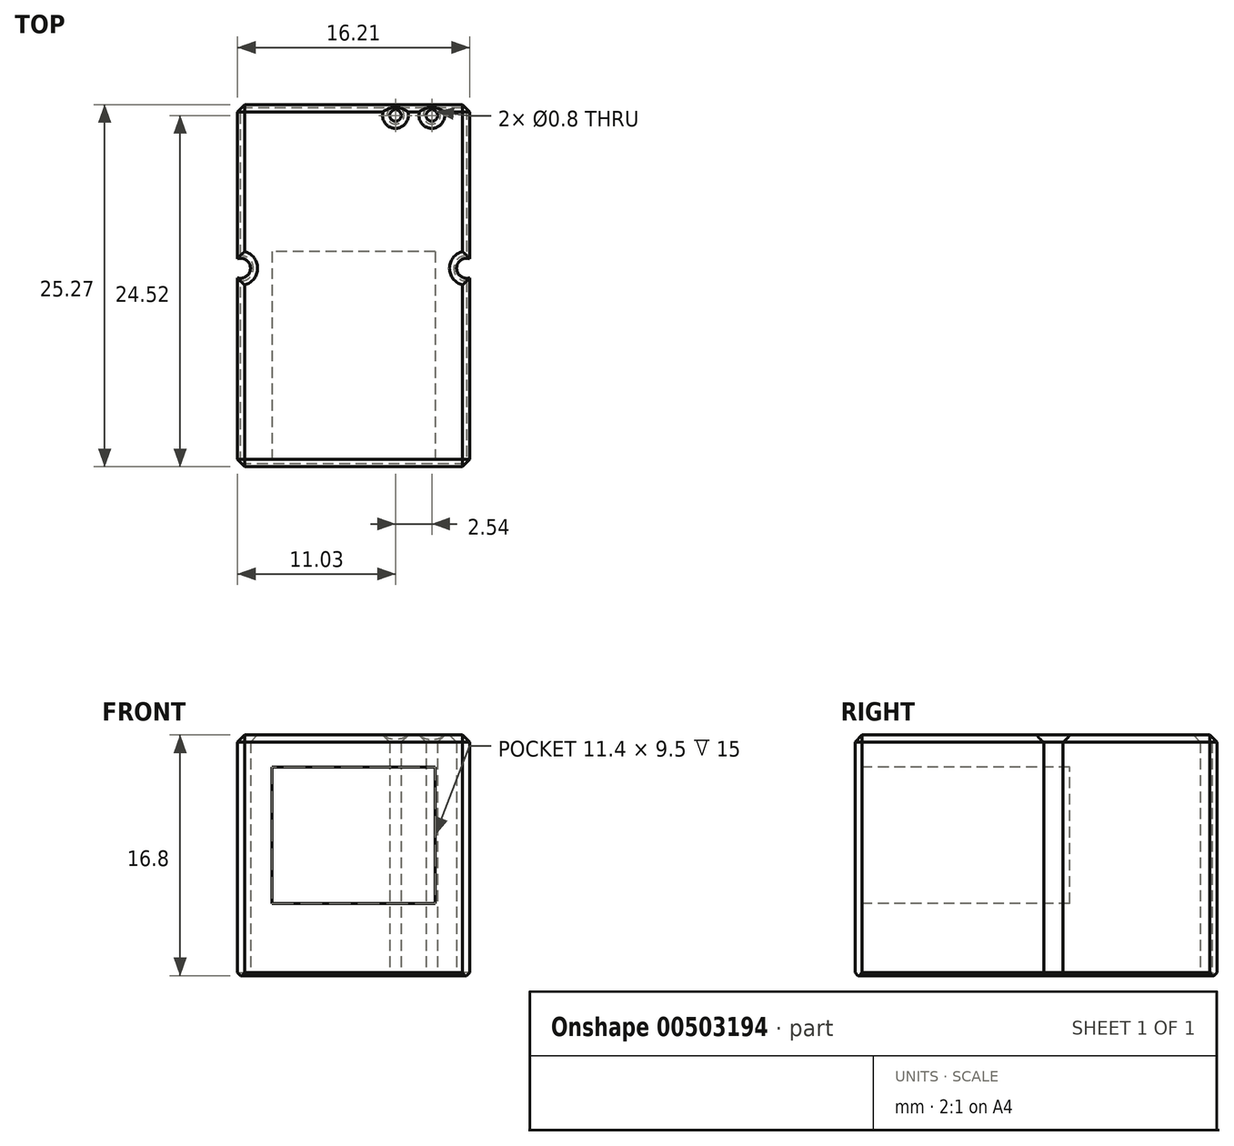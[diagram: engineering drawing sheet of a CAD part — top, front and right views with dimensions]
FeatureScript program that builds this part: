
annotation { "Feature Type Name" : "Feature", "Feature Type Description" : "" }
export const myFeature = defineFeature(function(context is Context, id is Id, definition is map)
    precondition{}
    {
        {
            var Q0;
            Q0=qCreatedBy(makeId("Top.planeOp"),FACE);
            var sketch = newSketch(context, id + "F0", { "sketchPlane" : qUnion([Q0])});
            skLineSegment(sketch, "E0.bottom", {"start": v(-12.55, 5.58) * mm, "end": v(3.66, 5.58) * mm});
            skLineSegment(sketch, "E0.top", {"start": v(-12.54, -19.7) * mm, "end": v(3.65, -19.7) * mm});
            skLineSegment(sketch, "E0.left", {"start": v(-12.54, 5.58) * mm, "end": v(-12.54, -19.7) * mm});
            skLineSegment(sketch, "E0.right", {"start": v(3.66, 5.58) * mm, "end": v(3.66, -19.7) * mm});
            skCircle(sketch, "E1", {"center": v(0, 0) * mm, "radius": 0.35 * mm});
            skCircle(sketch, "E2", {"center": v(-1.27, -2.54) * mm, "radius": 0.35 * mm});
            skLineSegment(sketch, "E3", {"start": v(-4.44, 5.58) * mm, "end": v(-4.45, -19.7) * mm, "construction": true});
            skCircle(sketch, "E4.1.0.0", {"center": v(-3.81, -2.54) * mm, "radius": 0.35 * mm});
            skCircle(sketch, "E4.1.0.1", {"center": v(-2.54, 0) * mm, "radius": 0.35 * mm});
            skCircle(sketch, "E4.2.0.0", {"center": v(-6.35, -2.54) * mm, "radius": 0.35 * mm});
            skCircle(sketch, "E4.2.0.1", {"center": v(-5.08, 0) * mm, "radius": 0.35 * mm});
            skCircle(sketch, "E4.3.0.0", {"center": v(-8.9, -2.54) * mm, "radius": 0.35 * mm});
            skCircle(sketch, "E4.3.0.1", {"center": v(-7.62, 0) * mm, "radius": 0.35 * mm});
            skLineSegment(sketch, "E4.direction1", {"start": v(-1.27, -2.54) * mm, "end": v(-3.81, -2.54) * mm, "construction": true});
            skCircle(sketch, "E5", {"center": v(-10.16, -8.9) * mm, "radius": 1.5 * mm});
            skCircle(sketch, "E6", {"center": v(1.27, -8.9) * mm, "radius": 1.5 * mm});
            skCircle(sketch, "E7", {"center": v(-12.34, -5.84) * mm, "radius": 0.7 * mm});
            skCircle(sketch, "E8", {"center": v(3.46, -5.84) * mm, "radius": 0.7 * mm});
            skPoint(sketch, "E8.centerSnap0", {"position": v(-4.44, -7.06) * mm});
            skCircle(sketch, "E9", {"center": v(-9.9, 4.83) * mm, "radius": 0.4 * mm});
            skCircle(sketch, "E10", {"center": v(-7.37, 4.83) * mm, "radius": 0.4 * mm});
            skCircle(sketch, "E11.MirrorC", {"center": v(-1.52, 4.83) * mm, "radius": 0.4 * mm});
            skCircle(sketch, "E12.MirrorC", {"center": v(1.02, 4.83) * mm, "radius": 0.4 * mm});
            skSolve(sketch);
        }
        {
            var Q0;
            {var subQ0=sQuery(id+"F0.wireOp",EDGE,"E7");var subQ1=sQuery(id+"F0.wireOp",EDGE,"E0.left");var subQ2=makeQuery(id+"F0.imprint","INTERSECT",VERTEX,{"disambiguationData":[OD(0.0)],"derivedFrom":[subQ1,subQ0]});Q0=makeQuery(id+"F0.imprint","IMPRINT",FACE,{"disambiguationData":[TD([[makeQuery(id+"F0.imprint","IMPRINT",EDGE,{"disambiguationData":[TD([[subQ2,-1.0]])],"derivedFrom":subQ1}),1.0]])]});}
            var Q1;
            {var subQ4=sQuery(id+"F0.wireOp",EDGE,"E0.bottom");Q1=makeQuery(id+"F0.imprint","IMPRINT",FACE,{"disambiguationData":[TD([[makeQuery(id+"F0.imprint","IMPRINT",EDGE,{"derivedFrom":subQ4}),-1.0]])]});}
            var Q2;
            Q2=makeQuery(id+"F0.imprint","IMPRINT",FACE,{"disambiguationData":[TD([[makeQuery(id+"F0.imprint","IMPRINT",EDGE,{"derivedFrom":sQuery(id+"F0.wireOp",EDGE,"E5")}),1.0]])]});
            var Q3;
            Q3=makeQuery(id+"F0.imprint","IMPRINT",FACE,{"disambiguationData":[TD([[makeQuery(id+"F0.imprint","IMPRINT",EDGE,{"derivedFrom":sQuery(id+"F0.wireOp",EDGE,"E6")}),1.0]])]});
            var Q4;
            {var subQ0=sQuery(id+"F0.wireOp",EDGE,"E8");var subQ1=sQuery(id+"F0.wireOp",EDGE,"E0.right");var subQ2=makeQuery(id+"F0.imprint","INTERSECT",VERTEX,{"disambiguationData":[OD(0.0)],"derivedFrom":[subQ1,subQ0]});Q4=makeQuery(id+"F0.imprint","IMPRINT",FACE,{"disambiguationData":[TD([[makeQuery(id+"F0.imprint","IMPRINT",EDGE,{"disambiguationData":[TD([[subQ2,-1.0]])],"derivedFrom":subQ1}),-1.0]])]});}
            var Q5;
            Q5=makeQuery(id+"F0.imprint","IMPRINT",FACE,{"disambiguationData":[TD([[makeQuery(id+"F0.imprint","IMPRINT",EDGE,{"derivedFrom":sQuery(id+"F0.wireOp",EDGE,"E2")}),1.0]])]});
            var Q6;
            Q6=makeQuery(id+"F0.imprint","IMPRINT",FACE,{"disambiguationData":[TD([[makeQuery(id+"F0.imprint","IMPRINT",EDGE,{"derivedFrom":sQuery(id+"F0.wireOp",EDGE,"E4.1.0.0")}),1.0]])]});
            var Q7;
            Q7=makeQuery(id+"F0.imprint","IMPRINT",FACE,{"disambiguationData":[TD([[makeQuery(id+"F0.imprint","IMPRINT",EDGE,{"derivedFrom":sQuery(id+"F0.wireOp",EDGE,"E4.2.0.0")}),1.0]])]});
            var Q8;
            Q8=makeQuery(id+"F0.imprint","IMPRINT",FACE,{"disambiguationData":[TD([[makeQuery(id+"F0.imprint","IMPRINT",EDGE,{"derivedFrom":sQuery(id+"F0.wireOp",EDGE,"E4.3.0.0")}),1.0]])]});
            var Q9;
            Q9=makeQuery(id+"F0.imprint","IMPRINT",FACE,{"disambiguationData":[TD([[makeQuery(id+"F0.imprint","IMPRINT",EDGE,{"derivedFrom":sQuery(id+"F0.wireOp",EDGE,"E4.3.0.1")}),1.0]])]});
            var Q10;
            Q10=makeQuery(id+"F0.imprint","IMPRINT",FACE,{"disambiguationData":[TD([[makeQuery(id+"F0.imprint","IMPRINT",EDGE,{"derivedFrom":sQuery(id+"F0.wireOp",EDGE,"E4.2.0.1")}),1.0]])]});
            var Q11;
            Q11=makeQuery(id+"F0.imprint","IMPRINT",FACE,{"disambiguationData":[TD([[makeQuery(id+"F0.imprint","IMPRINT",EDGE,{"derivedFrom":sQuery(id+"F0.wireOp",EDGE,"E4.1.0.1")}),1.0]])]});
            var Q12;
            Q12=makeQuery(id+"F0.imprint","IMPRINT",FACE,{"disambiguationData":[TD([[makeQuery(id+"F0.imprint","IMPRINT",EDGE,{"derivedFrom":sQuery(id+"F0.wireOp",EDGE,"E1")}),1.0]])]});
            var Q13;
            Q13=makeQuery(id+"F0.imprint","IMPRINT",FACE,{"disambiguationData":[TD([[makeQuery(id+"F0.imprint","IMPRINT",EDGE,{"derivedFrom":sQuery(id+"F0.wireOp",EDGE,"E12.MirrorC")}),-1.0]])]});
            var Q14;
            Q14=makeQuery(id+"F0.imprint","IMPRINT",FACE,{"disambiguationData":[TD([[makeQuery(id+"F0.imprint","IMPRINT",EDGE,{"derivedFrom":sQuery(id+"F0.wireOp",EDGE,"E11.MirrorC")}),-1.0]])]});
            var Q15;
            Q15=makeQuery(id+"F0.imprint","IMPRINT",FACE,{"disambiguationData":[TD([[makeQuery(id+"F0.imprint","IMPRINT",EDGE,{"derivedFrom":sQuery(id+"F0.wireOp",EDGE,"E10")}),1.0]])]});
            var Q16;
            Q16=makeQuery(id+"F0.imprint","IMPRINT",FACE,{"disambiguationData":[TD([[makeQuery(id+"F0.imprint","IMPRINT",EDGE,{"derivedFrom":sQuery(id+"F0.wireOp",EDGE,"E9")}),1.0]])]});
            extrude(context, id + "F1", {"entities" : qUnion([Q0, Q1, Q2, Q3, Q4, Q5, Q6, Q7, Q8, Q9, Q10, Q11, Q12, Q13, Q14, Q15, Q16]), "depth" : 13.5 * mm});
        }
        {
            var Q0;
            {var subQ0=sQuery(id+"F0.wireOp",EDGE,"E7");var subQ1=sQuery(id+"F0.wireOp",EDGE,"E0.left");var subQ2=makeQuery(id+"F0.imprint","INTERSECT",VERTEX,{"disambiguationData":[OD(0.0)],"derivedFrom":[subQ1,subQ0]});Q0=makeQuery(id+"F0.imprint","IMPRINT",FACE,{"disambiguationData":[TD([[makeQuery(id+"F0.imprint","IMPRINT",EDGE,{"disambiguationData":[TD([[subQ2,-1.0]])],"derivedFrom":subQ1}),1.0]])]});}
            var Q1;
            {var subQ0=sQuery(id+"F0.wireOp",EDGE,"E8");var subQ1=sQuery(id+"F0.wireOp",EDGE,"E0.right");var subQ2=makeQuery(id+"F0.imprint","INTERSECT",VERTEX,{"disambiguationData":[OD(0.0)],"derivedFrom":[subQ1,subQ0]});Q1=makeQuery(id+"F0.imprint","IMPRINT",FACE,{"disambiguationData":[TD([[makeQuery(id+"F0.imprint","IMPRINT",EDGE,{"disambiguationData":[TD([[subQ2,-1.0]])],"derivedFrom":subQ1}),-1.0]])]});}
            var Q2;
            Q2=makeQuery(id+"F0.imprint","IMPRINT",FACE,{"disambiguationData":[TD([[makeQuery(id+"F0.imprint","IMPRINT",EDGE,{"derivedFrom":sQuery(id+"F0.wireOp",EDGE,"E5")}),1.0]])]});
            var Q3;
            Q3=makeQuery(id+"F0.imprint","IMPRINT",FACE,{"disambiguationData":[TD([[makeQuery(id+"F0.imprint","IMPRINT",EDGE,{"derivedFrom":sQuery(id+"F0.wireOp",EDGE,"E6")}),1.0]])]});
            var Q4;
            Q4=makeQuery(id+"F0.imprint","IMPRINT",FACE,{"disambiguationData":[TD([[makeQuery(id+"F0.imprint","IMPRINT",EDGE,{"derivedFrom":sQuery(id+"F0.wireOp",EDGE,"E1")}),1.0]])]});
            var Q5;
            Q5=makeQuery(id+"F0.imprint","IMPRINT",FACE,{"disambiguationData":[TD([[makeQuery(id+"F0.imprint","IMPRINT",EDGE,{"derivedFrom":sQuery(id+"F0.wireOp",EDGE,"E2")}),1.0]])]});
            var Q6;
            Q6=makeQuery(id+"F0.imprint","IMPRINT",FACE,{"disambiguationData":[TD([[makeQuery(id+"F0.imprint","IMPRINT",EDGE,{"derivedFrom":sQuery(id+"F0.wireOp",EDGE,"E4.1.0.0")}),1.0]])]});
            var Q7;
            Q7=makeQuery(id+"F0.imprint","IMPRINT",FACE,{"disambiguationData":[TD([[makeQuery(id+"F0.imprint","IMPRINT",EDGE,{"derivedFrom":sQuery(id+"F0.wireOp",EDGE,"E4.1.0.1")}),1.0]])]});
            var Q8;
            Q8=makeQuery(id+"F0.imprint","IMPRINT",FACE,{"disambiguationData":[TD([[makeQuery(id+"F0.imprint","IMPRINT",EDGE,{"derivedFrom":sQuery(id+"F0.wireOp",EDGE,"E4.2.0.0")}),1.0]])]});
            var Q9;
            Q9=makeQuery(id+"F0.imprint","IMPRINT",FACE,{"disambiguationData":[TD([[makeQuery(id+"F0.imprint","IMPRINT",EDGE,{"derivedFrom":sQuery(id+"F0.wireOp",EDGE,"E4.2.0.1")}),1.0]])]});
            var Q10;
            Q10=makeQuery(id+"F0.imprint","IMPRINT",FACE,{"disambiguationData":[TD([[makeQuery(id+"F0.imprint","IMPRINT",EDGE,{"derivedFrom":sQuery(id+"F0.wireOp",EDGE,"E4.3.0.0")}),1.0]])]});
            var Q11;
            Q11=makeQuery(id+"F0.imprint","IMPRINT",FACE,{"disambiguationData":[TD([[makeQuery(id+"F0.imprint","IMPRINT",EDGE,{"derivedFrom":sQuery(id+"F0.wireOp",EDGE,"E4.3.0.1")}),1.0]])]});
            var Q12;
            Q12=makeQuery(id+"F0.imprint","IMPRINT",FACE,{"disambiguationData":[TD([[makeQuery(id+"F0.imprint","IMPRINT",EDGE,{"derivedFrom":sQuery(id+"F0.wireOp",EDGE,"E11.MirrorC")}),-1.0]])]});
            var Q13;
            Q13=makeQuery(id+"F0.imprint","IMPRINT",FACE,{"disambiguationData":[TD([[makeQuery(id+"F0.imprint","IMPRINT",EDGE,{"derivedFrom":sQuery(id+"F0.wireOp",EDGE,"E12.MirrorC")}),-1.0]])]});
            var Q14;
            Q14=makeQuery(id+"F0.imprint","IMPRINT",FACE,{"disambiguationData":[TD([[makeQuery(id+"F0.imprint","IMPRINT",EDGE,{"derivedFrom":sQuery(id+"F0.wireOp",EDGE,"E10")}),1.0]])]});
            var Q15;
            Q15=makeQuery(id+"F0.imprint","IMPRINT",FACE,{"disambiguationData":[TD([[makeQuery(id+"F0.imprint","IMPRINT",EDGE,{"derivedFrom":sQuery(id+"F0.wireOp",EDGE,"E9")}),1.0]])]});
            extrude(context, id + "F2", {"entities" : qUnion([Q0, Q1, Q2, Q3, Q4, Q5, Q6, Q7, Q8, Q9, Q10, Q11, Q12, Q13, Q14, Q15]), "operationType" : NewBodyOperationType.ADD, "oppositeDirection" : true, "depth" : 3.3 * mm});
        }
        {
            var Q0;
            Q0=makeQuery(id+"F2.opExtrude","CAP_FACE",FACE,{"disambiguationData":[OSD([sQuery(id+"F0.wireOp",EDGE,"E6")])],"isStart":false});
            var Q1;
            Q1=makeQuery(id+"F2.opExtrude","CAP_FACE",FACE,{"disambiguationData":[OSD([sQuery(id+"F0.wireOp",EDGE,"E5")])],"isStart":false});
            var Q2;
            Q2=makeQuery(id+"F2.opExtrude","CAP_FACE",FACE,{"disambiguationData":[OSD([sQuery(id+"F0.wireOp",EDGE,"E7")])],"isStart":false});
            var Q3;
            Q3=makeQuery(id+"F2.opExtrude","CAP_FACE",FACE,{"disambiguationData":[OSD([sQuery(id+"F0.wireOp",EDGE,"E1")])],"isStart":false});
            var Q4;
            Q4=makeQuery(id+"F2.opExtrude","CAP_FACE",FACE,{"disambiguationData":[OSD([sQuery(id+"F0.wireOp",EDGE,"E4.1.0.1")])],"isStart":false});
            var Q5;
            Q5=makeQuery(id+"F2.opExtrude","CAP_FACE",FACE,{"disambiguationData":[OSD([sQuery(id+"F0.wireOp",EDGE,"E2")])],"isStart":false});
            var Q6;
            Q6=makeQuery(id+"F2.opExtrude","CAP_FACE",FACE,{"disambiguationData":[OSD([sQuery(id+"F0.wireOp",EDGE,"E4.1.0.0")])],"isStart":false});
            var Q7;
            Q7=makeQuery(id+"F2.opExtrude","CAP_FACE",FACE,{"disambiguationData":[OSD([sQuery(id+"F0.wireOp",EDGE,"E4.2.0.0")])],"isStart":false});
            var Q8;
            Q8=makeQuery(id+"F2.opExtrude","CAP_FACE",FACE,{"disambiguationData":[OSD([sQuery(id+"F0.wireOp",EDGE,"E4.3.0.0")])],"isStart":false});
            var Q9;
            Q9=makeQuery(id+"F2.opExtrude","CAP_FACE",FACE,{"disambiguationData":[OSD([sQuery(id+"F0.wireOp",EDGE,"E4.2.0.1")])],"isStart":false});
            var Q10;
            Q10=makeQuery(id+"F2.opExtrude","CAP_FACE",FACE,{"disambiguationData":[OSD([sQuery(id+"F0.wireOp",EDGE,"E4.3.0.1")])],"isStart":false});
            var Q11;
            Q11=makeQuery(id+"F2.opExtrude","CAP_FACE",FACE,{"disambiguationData":[OSD([sQuery(id+"F0.wireOp",EDGE,"E10")])],"isStart":false});
            var Q12;
            Q12=makeQuery(id+"F2.opExtrude","CAP_FACE",FACE,{"disambiguationData":[OSD([sQuery(id+"F0.wireOp",EDGE,"E11.MirrorC")])],"isStart":false});
            var Q13;
            Q13=makeQuery(id+"F2.opExtrude","CAP_FACE",FACE,{"disambiguationData":[OSD([sQuery(id+"F0.wireOp",EDGE,"E12.MirrorC")])],"isStart":false});
            var Q14;
            Q14=makeQuery(id+"F2.opExtrude","CAP_FACE",FACE,{"disambiguationData":[OSD([sQuery(id+"F0.wireOp",EDGE,"E9")])],"isStart":false});
            var Q15;
            Q15=makeQuery(id+"F2.opExtrude","CAP_FACE",FACE,{"disambiguationData":[OSD([sQuery(id+"F0.wireOp",EDGE,"E8")])],"isStart":false});
            chamfer(context, id + "F3", {"entities" : qUnion([Q0, Q1, Q2, Q3, Q4, Q5, Q6, Q7, Q8, Q9, Q10, Q11, Q12, Q13, Q14, Q15]), "width" : .2 * mm, "tangentPropagation" : true});
        }
        {
            var Q0;
            Q0=makeQuery(id+"F1.opExtrude","CAP_FACE",FACE,{"disambiguationData":[OSD([sQuery(id+"F0.wireOp",EDGE,"E0.bottom"),sQuery(id+"F0.wireOp",EDGE,"E0.top"),sQuery(id+"F0.wireOp",EDGE,"E0.left"),sQuery(id+"F0.wireOp",EDGE,"E0.right")])],"isStart":false});
            var Q1;
            Q1=makeQuery(id+"F1.opExtrude","SWEPT_EDGE",EDGE,{"disambiguationData":[OSD([sQuery(id+"F0.wireOp",EDGE,"E0.bottom"),sQuery(id+"F0.wireOp",EDGE,"E0.right")])]});
            var Q2;
            Q2=makeQuery(id+"F1.opExtrude","SWEPT_EDGE",EDGE,{"disambiguationData":[OSD([sQuery(id+"F0.wireOp",EDGE,"E0.bottom"),sQuery(id+"F0.wireOp",EDGE,"E0.left")])]});
            var Q3;
            Q3=makeQuery(id+"F1.opExtrude","SWEPT_EDGE",EDGE,{"disambiguationData":[OSD([sQuery(id+"F0.wireOp",EDGE,"E0.top"),sQuery(id+"F0.wireOp",EDGE,"E0.right")])]});
            var Q4;
            Q4=makeQuery(id+"F1.opExtrude","SWEPT_EDGE",EDGE,{"disambiguationData":[OSD([sQuery(id+"F0.wireOp",EDGE,"E0.top"),sQuery(id+"F0.wireOp",EDGE,"E0.left")])]});
            chamfer(context, id + "F4", {"entities" : qUnion([Q0, Q1, Q2, Q3, Q4]), "width" : .5 * mm, "tangentPropagation" : true});
        }
        {
            var Q0;
            Q0=makeQuery(id+"F1.opExtrude","SWEPT_FACE",FACE,{"disambiguationData":[OSD([sQuery(id+"F0.wireOp",EDGE,"E0.top")])]});
            var sketch = newSketch(context, id + "F5", { "sketchPlane" : qUnion([Q0])});
            skLineSegment(sketch, "E13.bottom", {"start": v(1.26, 1.75) * mm, "end": v(-10.14, 1.75) * mm});
            skLineSegment(sketch, "E13.top", {"start": v(1.26, 11.25) * mm, "end": v(-10.14, 11.25) * mm});
            skLineSegment(sketch, "E13.left", {"start": v(1.26, 1.75) * mm, "end": v(1.26, 11.25) * mm});
            skLineSegment(sketch, "E13.right", {"start": v(-10.14, 1.75) * mm, "end": v(-10.14, 11.25) * mm});
            skPoint(sketch, "E13.middle", {"position": v(-4.44, 6.5) * mm});
            skPoint(sketch, "E13.middle.positionSnap0", {"position": v(3.16, 6.5) * mm});
            skPoint(sketch, "E13.middle.positionSnap1", {"position": v(-4.44, 0) * mm});
            skPoint(sketch, "E13.centerSnap0", {"position": v(3.16, 6.5) * mm});
            skPoint(sketch, "E13.centerSnap1", {"position": v(-4.44, 0) * mm});
            skLineSegment(sketch, "E14.bottom", {"start": v(-2.54, 11.25) * mm, "end": v(-6.34, 11.25) * mm});
            skLineSegment(sketch, "E14.top", {"start": v(-2.54, 12.6) * mm, "end": v(-6.34, 12.6) * mm});
            skLineSegment(sketch, "E14.left", {"start": v(-2.54, 11.25) * mm, "end": v(-2.54, 12.6) * mm});
            skLineSegment(sketch, "E14.right", {"start": v(-6.34, 11.25) * mm, "end": v(-6.34, 12.6) * mm});
            skPoint(sketch, "E14.middle", {"position": v(-4.44, 11.93) * mm});
            skPoint(sketch, "E14.middle.positionSnap0", {"position": v(-4.44, 13) * mm});
            skPoint(sketch, "E14.centerSnap0", {"position": v(-4.44, 13) * mm});
            skSolve(sketch);
        }
        {
            var Q0;
            Q0=makeQuery(id+"F5.imprint","IMPRINT",FACE,{"disambiguationData":[TD([[makeQuery(id+"F5.imprint","IMPRINT",EDGE,{"derivedFrom":sQuery(id+"F5.wireOp",EDGE,"E14.bottom")}),-1.0]])]});
            var Q1;
            Q1=makeQuery(id+"F5.imprint","IMPRINT",FACE,{"disambiguationData":[TD([[makeQuery(id+"F5.imprint","IMPRINT",EDGE,{"derivedFrom":sQuery(id+"F5.wireOp",EDGE,"E13.bottom")}),-1.0]])]});
            extrude(context, id + "F6", {"entities" : qUnion([Q0, Q1]), "operationType" : NewBodyOperationType.REMOVE, "oppositeDirection" : true, "depth" : 15 * mm});
        }
    });
